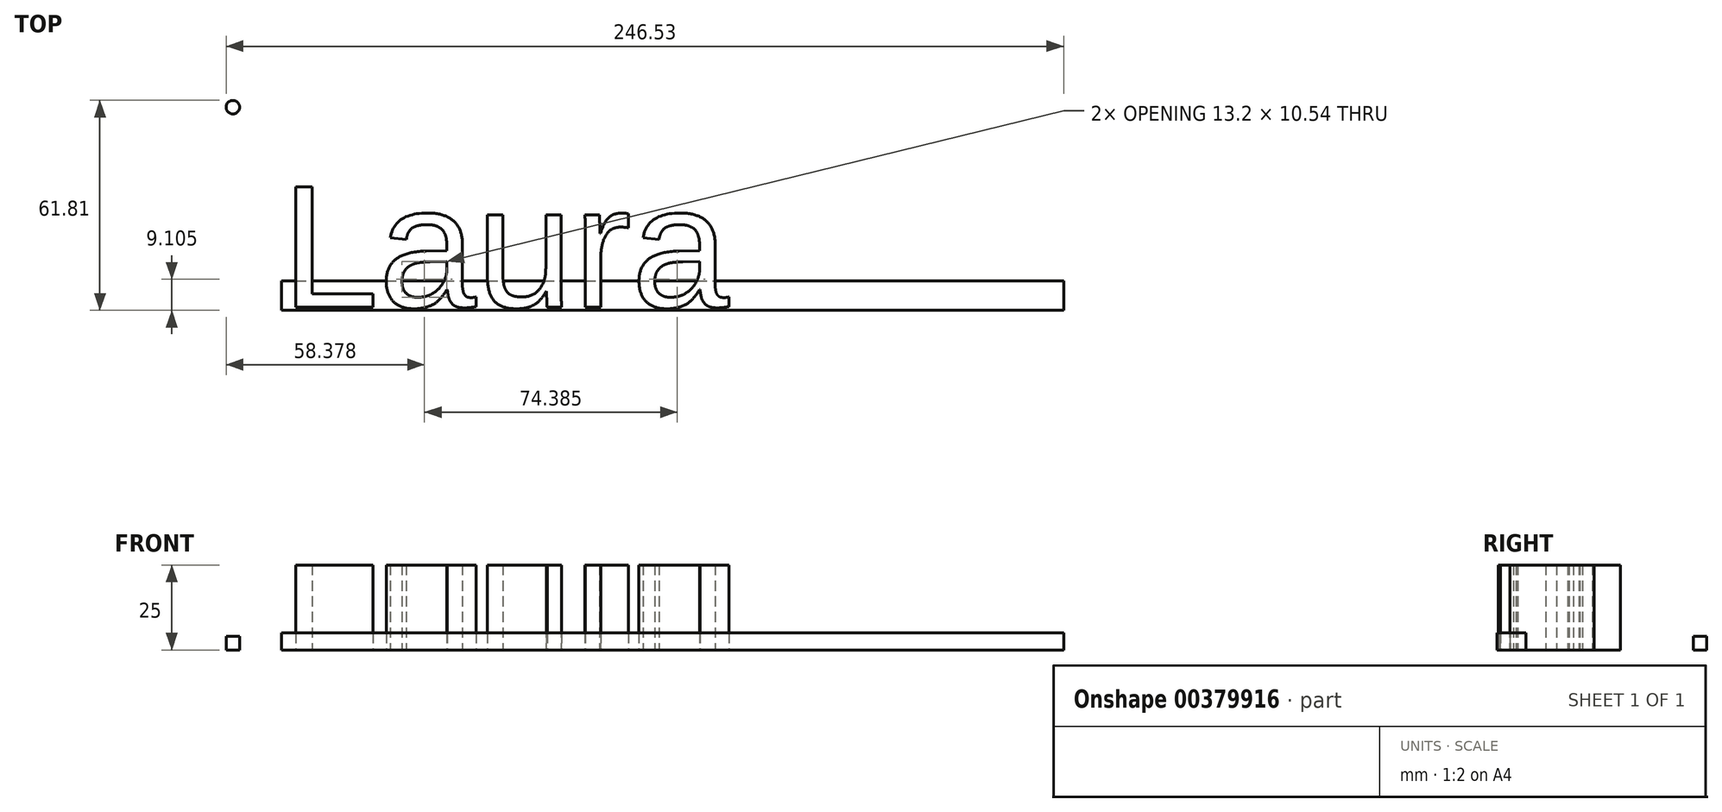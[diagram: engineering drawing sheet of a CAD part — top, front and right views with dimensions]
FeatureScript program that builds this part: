
annotation { "Feature Type Name" : "Feature", "Feature Type Description" : "" }
export const myFeature = defineFeature(function(context is Context, id is Id, definition is map)
    precondition{}
    {
        {
            var Q0;
            Q0=qCreatedBy(makeId("Top.planeOp"),FACE);
            var sketch = newSketch(context, id + "F0", { "sketchPlane" : qUnion([Q0])});
            skCircle(sketch, "E0", {"center": v(-14.32, 14.84) * mm, "radius": 2 * mm});
            skSolve(sketch);
        }
        {
            var Q0;
            Q0 = qSketchRegion(id + "F0", true);
            extrude(context, id + "F1", {"entities" : qUnion([Q0]), "depth" : 4 * mm});
        }
        {
            var Q0;
            Q0=qCreatedBy(makeId("Top.planeOp"),FACE);
            var sketch = newSketch(context, id + "F2", { "sketchPlane" : qUnion([Q0])});
            skText(sketch, "E1", { "text": "Laura", "fontName": "Arimo-Regular.ttf"});
            const initialGuessF2  = {"E1": [0, -0.04402, 1, 0, 0.03706]};
            skSetInitialGuess(sketch, initialGuessF2);
            skSolve(sketch);
        }
        {
            var Q0;
            Q0=qCreatedBy(makeId("Top.planeOp"),FACE);
            var sketch = newSketch(context, id + "F3", { "sketchPlane" : qUnion([Q0])});
            skLineSegment(sketch, "E2.bottom", {"start": v(0, -36.36) * mm, "end": v(230.2, -36.36) * mm});
            skLineSegment(sketch, "E2.top", {"start": v(0, -44.97) * mm, "end": v(230.2, -44.97) * mm});
            skLineSegment(sketch, "E2.left", {"start": v(0, -36.36) * mm, "end": v(0, -44.97) * mm});
            skLineSegment(sketch, "E2.right", {"start": v(230.2, -36.36) * mm, "end": v(230.2, -44.97) * mm});
            skSolve(sketch);
        }
        {
            var Q0;
            Q0 = qSketchRegion(id + "F2", true);
            extrude(context, id + "F4", {"entities" : qUnion([Q0]), "depth" : 25 * mm});
        }
        {
            var Q0;
            Q0=makeQuery(id+"F3.imprint","IMPRINT",FACE,{"disambiguationData":[TD([[makeQuery(id+"F3.imprint","IMPRINT",EDGE,{"derivedFrom":sQuery(id+"F3.wireOp",EDGE,"E2.bottom")}),-1.0]])]});
            extrude(context, id + "F5", {"entities" : qUnion([Q0]), "depth" : 5 * mm});
        }
    });
